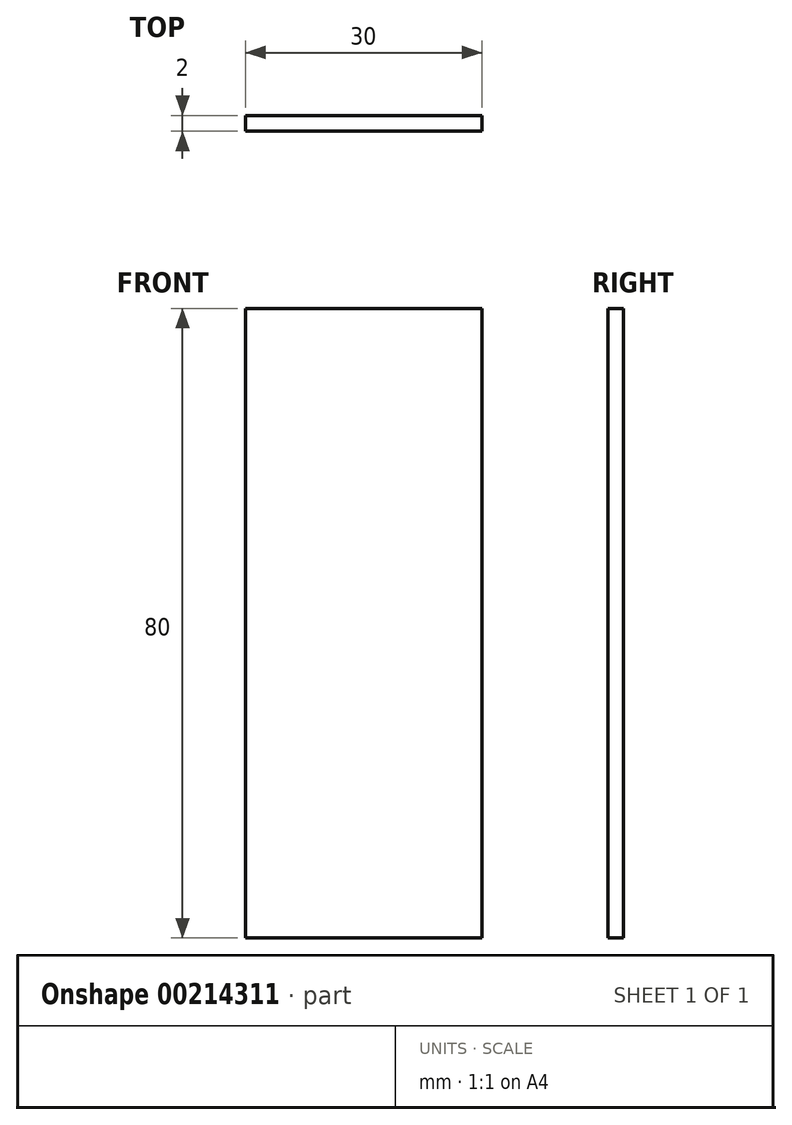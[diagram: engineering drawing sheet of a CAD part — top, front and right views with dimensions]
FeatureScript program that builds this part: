
annotation { "Feature Type Name" : "Feature", "Feature Type Description" : "" }
export const myFeature = defineFeature(function(context is Context, id is Id, definition is map)
    precondition{}
    {
        {
            var Q0;
            Q0=qCreatedBy(makeId("Front.planeOp"),FACE);
            var sketch = newSketch(context, id + "F0", { "sketchPlane" : qUnion([Q0])});
            skLineSegment(sketch, "E0.bottom", {"start": v(15, 40) * mm, "end": v(-15, 40) * mm});
            skLineSegment(sketch, "E0.top", {"start": v(15, -40) * mm, "end": v(-15, -40) * mm});
            skLineSegment(sketch, "E0.left", {"start": v(15, 40) * mm, "end": v(15, -40) * mm});
            skLineSegment(sketch, "E0.right", {"start": v(-15, 40) * mm, "end": v(-15, -40) * mm});
            skPoint(sketch, "E0.middle", {"position": v(0, 0) * mm});
            skSolve(sketch);
        }
        {
            var Q0;
            Q0 = qSketchRegion(id + "F0", true);
            extrude(context, id + "F1", {"entities" : qUnion([Q0]), "depth" : 2 * mm});
        }
    });
